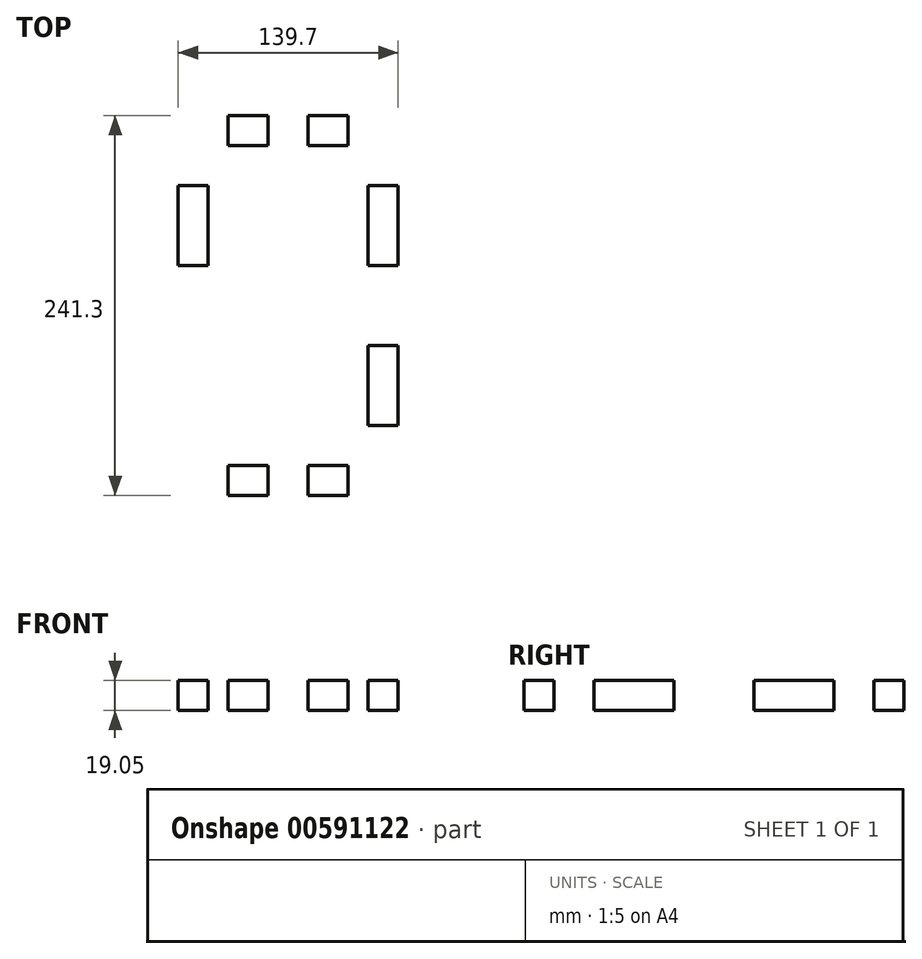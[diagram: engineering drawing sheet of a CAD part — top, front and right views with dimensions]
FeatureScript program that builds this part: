
annotation { "Feature Type Name" : "Feature", "Feature Type Description" : "" }
export const myFeature = defineFeature(function(context is Context, id is Id, definition is map)
    precondition{}
    {
        {
            var Q0;
            Q0=qCreatedBy(makeId("Top.planeOp"),FACE);
            var sketch = newSketch(context, id + "F0", { "sketchPlane" : qUnion([Q0])});
            skLineSegment(sketch, "E0.bottom", {"start": v(-16.05, 111.49) * mm, "end": v(85.55, 111.49) * mm});
            skLineSegment(sketch, "E0.top", {"start": v(-16.05, -91.71) * mm, "end": v(85.55, -91.71) * mm});
            skLineSegment(sketch, "E0.left", {"start": v(-16.05, 111.49) * mm, "end": v(-16.05, -91.71) * mm});
            skLineSegment(sketch, "E0.right", {"start": v(85.55, 111.49) * mm, "end": v(85.55, -91.71) * mm});
            skLineSegment(sketch, "E1", {"start": v(-16.05, -91.71) * mm, "end": v(-3.35, -91.71) * mm});
            skLineSegment(sketch, "E2", {"start": v(85.55, -91.71) * mm, "end": v(72.85, -91.71) * mm});
            skLineSegment(sketch, "E3", {"start": v(-16.05, 9.89) * mm, "end": v(85.55, 9.89) * mm, "construction": true});
            skLineSegment(sketch, "E4", {"start": v(-16.05, -91.71) * mm, "end": v(-16.05, -66.31) * mm});
            skLineSegment(sketch, "E5", {"start": v(-16.05, -66.31) * mm, "end": v(-16.05, -32.83) * mm});
            skLineSegment(sketch, "E6", {"start": v(-16.05, -66.31) * mm, "end": v(-35.1, -66.31) * mm});
            skLineSegment(sketch, "E7", {"start": v(-35.1, -66.31) * mm, "end": v(-35.1, -15.51) * mm});
            skLineSegment(sketch, "E8", {"start": v(-35.1, -15.51) * mm, "end": v(-16.05, -15.51) * mm});
            skLineSegment(sketch, "E9", {"start": v(-16.05, -15.51) * mm, "end": v(-16.05, 35.29) * mm});
            skLineSegment(sketch, "E10", {"start": v(-16.05, 35.29) * mm, "end": v(-35.1, 35.29) * mm});
            skLineSegment(sketch, "E11", {"start": v(-35.1, 35.29) * mm, "end": v(-35.1, 86.09) * mm});
            skLineSegment(sketch, "E12", {"start": v(-35.1, 86.09) * mm, "end": v(-16.05, 86.09) * mm});
            skLineSegment(sketch, "E13", {"start": v(-16.05, 86.09) * mm, "end": v(-16.05, 111.49) * mm});
            skLineSegment(sketch, "E14", {"start": v(-16.05, 111.49) * mm, "end": v(-16.05, 150.7) * mm, "construction": true});
            skLineSegment(sketch, "E15", {"start": v(-16.05, 150.7) * mm, "end": v(85.55, 150.7) * mm, "construction": true});
            skLineSegment(sketch, "E16", {"start": v(85.55, 150.7) * mm, "end": v(85.55, -178.16) * mm, "construction": true});
            skLineSegment(sketch, "E17", {"start": v(85.55, -91.71) * mm, "end": v(85.55, -66.31) * mm, "construction": true});
            skLineSegment(sketch, "E18", {"start": v(85.55, -66.31) * mm, "end": v(104.6, -66.31) * mm});
            skLineSegment(sketch, "E19", {"start": v(104.6, -66.31) * mm, "end": v(104.6, -15.51) * mm});
            skLineSegment(sketch, "E20", {"start": v(104.6, -15.51) * mm, "end": v(85.55, -15.51) * mm});
            skLineSegment(sketch, "E21", {"start": v(85.55, -15.51) * mm, "end": v(85.55, 29.33) * mm, "construction": true});
            skLineSegment(sketch, "E22", {"start": v(85.55, 35.29) * mm, "end": v(104.6, 35.29) * mm});
            skLineSegment(sketch, "E23", {"start": v(104.6, 35.29) * mm, "end": v(104.6, 86.09) * mm});
            skLineSegment(sketch, "E24", {"start": v(104.6, 86.09) * mm, "end": v(85.55, 86.09) * mm});
            skLineSegment(sketch, "E25", {"start": v(-3.35, -91.71) * mm, "end": v(-3.35, -110.76) * mm});
            skLineSegment(sketch, "E26", {"start": v(-3.35, -110.76) * mm, "end": v(22.05, -110.76) * mm});
            skLineSegment(sketch, "E27", {"start": v(22.05, -110.76) * mm, "end": v(22.05, -91.71) * mm});
            skLineSegment(sketch, "E28", {"start": v(22.05, -110.76) * mm, "end": v(47.45, -110.76) * mm, "construction": true});
            skLineSegment(sketch, "E29", {"start": v(47.45, -91.71) * mm, "end": v(47.45, -110.76) * mm});
            skLineSegment(sketch, "E30", {"start": v(47.45, -110.76) * mm, "end": v(72.85, -110.76) * mm});
            skLineSegment(sketch, "E31", {"start": v(72.85, -110.76) * mm, "end": v(72.85, -91.71) * mm});
            skLineSegment(sketch, "E32.MirrorCS", {"start": v(22.05, 130.54) * mm, "end": v(22.05, 111.49) * mm});
            skLineSegment(sketch, "E33.MirrorCS", {"start": v(-3.35, 130.54) * mm, "end": v(22.05, 130.54) * mm});
            skLineSegment(sketch, "E34.MirrorCS", {"start": v(47.45, 130.54) * mm, "end": v(72.85, 130.54) * mm});
            skLineSegment(sketch, "E35.MirrorCS", {"start": v(47.45, 111.49) * mm, "end": v(47.45, 130.54) * mm});
            skLineSegment(sketch, "E36.MirrorCS", {"start": v(72.85, 130.54) * mm, "end": v(72.85, 111.49) * mm});
            skLineSegment(sketch, "E37.MirrorCS", {"start": v(-3.35, 111.49) * mm, "end": v(-3.35, 130.54) * mm});
            skSolve(sketch);
        }
        {
            var Q0;
            {var subQ2=sQuery(id+"F0.wireOp",EDGE,"E10");Q0=makeQuery(id+"F0.imprint","IMPRINT",FACE,{"disambiguationData":[TD([[makeQuery(id+"F0.imprint","IMPRINT",EDGE,{"derivedFrom":subQ2}),-1.0]])]});}
            var Q1;
            {var subQ11=sQuery(id+"F0.wireOp",EDGE,"E1");Q1=makeQuery(id+"F0.imprint","IMPRINT",FACE,{"disambiguationData":[TD([[makeQuery(id+"F0.imprint","IMPRINT",EDGE,{"derivedFrom":subQ11}),1.0]])]});}
            var Q2;
            Q2=makeQuery(id+"F0.imprint","IMPRINT",FACE,{"disambiguationData":[TD([[makeQuery(id+"F0.imprint","IMPRINT",EDGE,{"derivedFrom":sQuery(id+"F0.wireOp",EDGE,"22bb1522-f6a5-4ca9-ab32-25fa2ed326b60.MirrorCS")}),-1.0]])]});
            var Q3;
            {var subQ0=sQuery(id+"F0.wireOp",EDGE,"fcdb45a5-25bd-41c4-bb1e-494c9c4a592b0.MirrorCS");Q3=makeQuery(id+"F0.imprint","IMPRINT",FACE,{"disambiguationData":[TD([[makeQuery(id+"F0.imprint","IMPRINT",EDGE,{"derivedFrom":subQ0}),-1.0]])]});}
            var Q4;
            {var subQ0=sQuery(id+"F0.wireOp",EDGE,"d0e553cf-9a45-49b6-8169-8e764b24579e0.MirrorCS");Q4=makeQuery(id+"F0.imprint","IMPRINT",FACE,{"disambiguationData":[TD([[makeQuery(id+"F0.imprint","IMPRINT",EDGE,{"derivedFrom":subQ0}),1.0]])]});}
            var Q5;
            {var subQ0=sQuery(id+"F0.wireOp",EDGE,"dcd3e8c7-ddd1-47d4-bc8c-4fdcb6949fbf0.MirrorCS");Q5=makeQuery(id+"F0.imprint","IMPRINT",FACE,{"disambiguationData":[TD([[makeQuery(id+"F0.imprint","IMPRINT",EDGE,{"derivedFrom":subQ0}),1.0]])]});}
            var Q6;
            {var subQ2=sQuery(id+"F0.wireOp",EDGE,"pHAPilBh-mq0K-QK4V-Zm0S-8bwN6dqoe8QB");Q6=makeQuery(id+"F0.imprint","IMPRINT",FACE,{"disambiguationData":[TD([[makeQuery(id+"F0.imprint","IMPRINT",EDGE,{"derivedFrom":subQ2}),1.0]])]});}
            var Q7;
            {var subQ0=sQuery(id+"F0.wireOp",EDGE,"4DMsL13P-fTkp-taxY-rDtn-H75gk7SVvTg4");Q7=makeQuery(id+"F0.imprint","IMPRINT",FACE,{"disambiguationData":[TD([[makeQuery(id+"F0.imprint","IMPRINT",EDGE,{"derivedFrom":subQ0}),1.0]])]});}
            var Q8;
            {var subQ0=sQuery(id+"F0.wireOp",EDGE,"E5");Q8=makeQuery(id+"F0.imprint","IMPRINT",FACE,{"disambiguationData":[TD([[makeQuery(id+"F0.imprint","IMPRINT",EDGE,{"derivedFrom":subQ0}),1.0]])]});}
            var Q9;
            {var subQ0=sQuery(id+"F0.wireOp",EDGE,"E25");Q9=makeQuery(id+"F0.imprint","IMPRINT",FACE,{"disambiguationData":[TD([[makeQuery(id+"F0.imprint","IMPRINT",EDGE,{"derivedFrom":subQ0}),1.0]])]});}
            var Q10;
            {var subQ2=sQuery(id+"F0.wireOp",EDGE,"E29");Q10=makeQuery(id+"F0.imprint","IMPRINT",FACE,{"disambiguationData":[TD([[makeQuery(id+"F0.imprint","IMPRINT",EDGE,{"derivedFrom":subQ2}),1.0]])]});}
            var Q11;
            {var subQ0=sQuery(id+"F0.wireOp",EDGE,"E18");Q11=makeQuery(id+"F0.imprint","IMPRINT",FACE,{"disambiguationData":[TD([[makeQuery(id+"F0.imprint","IMPRINT",EDGE,{"derivedFrom":subQ0}),1.0]])]});}
            var Q12;
            {var subQ0=sQuery(id+"F0.wireOp",EDGE,"E22");Q12=makeQuery(id+"F0.imprint","IMPRINT",FACE,{"disambiguationData":[TD([[makeQuery(id+"F0.imprint","IMPRINT",EDGE,{"derivedFrom":subQ0}),1.0]])]});}
            var Q13;
            Q13=makeQuery(id+"F0.imprint","IMPRINT",FACE,{"disambiguationData":[TD([[makeQuery(id+"F0.imprint","IMPRINT",EDGE,{"derivedFrom":sQuery(id+"F0.wireOp",EDGE,"E34.MirrorCS")}),-1.0]])]});
            var Q14;
            {var subQ0=sQuery(id+"F0.wireOp",EDGE,"E32.MirrorCS");Q14=makeQuery(id+"F0.imprint","IMPRINT",FACE,{"disambiguationData":[TD([[makeQuery(id+"F0.imprint","IMPRINT",EDGE,{"derivedFrom":subQ0}),-1.0]])]});}
            extrude(context, id + "F1", {"entities" : qUnion([Q0, Q1, Q2, Q3, Q4, Q5, Q6, Q7, Q8, Q9, Q10, Q11, Q12, Q13, Q14]), "depth" : 19.05 * mm, "offsetDistance" : 25.4 * mm});
        }
    });
